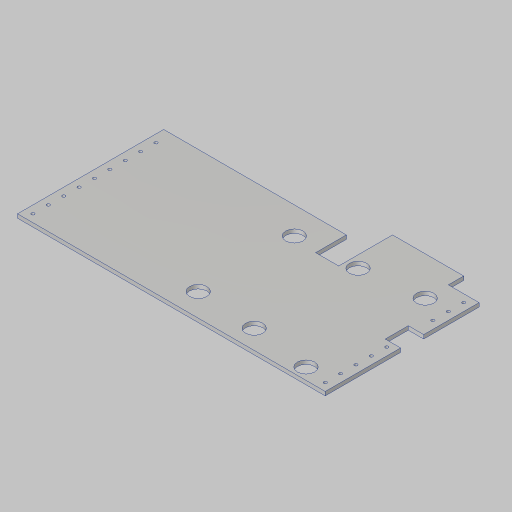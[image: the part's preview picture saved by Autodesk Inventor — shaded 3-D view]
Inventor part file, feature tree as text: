
AUTODESK INVENTOR PART (.ipt)
format: ipt  version: 2023.5 (Build 275446000, 446)  size: 199,680 bytes
history: native  units: in
note: dims shown in document units (in); Inventor stores cm internally (conversion verified against a paired STEP export)
features: sketch x4, extrude x3, projected_geometry x2, hole x1
ambient origin geometry x8: Origin, YZ Plane, XZ Plane, XY Plane, X Axis, Y Axis, Z Axis, Center Point
bodies: Solid1 (feature_tree)
feature tree (10):
  extrude  "Extrusion1"  Depth=11.0in
  hole  "Hole1"  [1 undecoded]
  extrude  "Extrusion2"  Depth=0.5in
  extrude  "Extrusion3"  Depth=1.0in TaperAngle=0.0deg
  sketch  "Sketch1"  dims[d0=20.0in d1=11.0in]
  sketch  "Sketch2"  dims[d2=0.25in d3=0.0in d4=0.5in]
  sketch  "Sketch3"  dims[d5=0.5in d6=0.5in]
  projected_geometry  "Projected Loop1"
  sketch  "Sketch4"  dims[d7=4.3307in d9=1.0in d10=0.3937in d12=1.0in d14=0.201in d15=0.38in d16=0.385in d17=0.25in d18=0.5635in d19=1.0in d20=0.8108in d24=1.0in d25=0.0in d28=4.5in d29=12.0in d30=1.0in d31=2.0in d32=1.125in d33=4.0in d34=2.5in d35=3.25in d36=0.125in d37=3.8976in d38=0.75in d39=1.0in d40=0.0in d42=8.125in d43=1.5in d44=3.5in d45=6.625in d46=1.0in d47=1.5in d48=4.9in d49=2.0in d50=0.125in d51=3.8976in]
  projected_geometry  "Projected Loop2"
note: 1 required parameter value undecoded (feature->parameter linkage not recoverable at this tier; creation-order binding heuristic only, values carry confidence <= 0.55)
